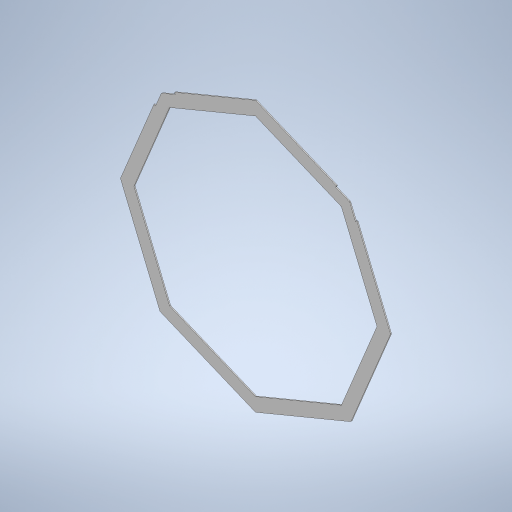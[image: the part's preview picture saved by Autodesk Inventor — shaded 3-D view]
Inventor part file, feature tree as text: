
AUTODESK INVENTOR PART (.ipt)
format: ipt  version: 2024.2 (Build 282272000, 272)  size: 311,296 bytes
history: native  units: mm
features: sketch x2, sheet_metal_op x1, extrude x1, mirror x1, other x1
ambient origin geometry x8: Origin, YZ Plane, XZ Plane, XY Plane, X Axis, Y Axis, Z Axis, Center Point
bodies: Body1 (feature_tree)
feature tree (6):
  sheet_metal_op  "Face2"
  extrude  "Extrusion1"  Depth=25.0mm
  mirror  "Mirror1"
  sketch  "Sketch1"  dims[d18=500.0mm d19=25.0mm]
  other  "Plate2"
  sketch  "Sketch3"  dims[d20=3.0mm d21=2.0mm d22=3.0mm d23=3.5mm d24=3.0mm d25=29.0mm d26=3.5mm d27=10.0mm d28=0.0mm]
